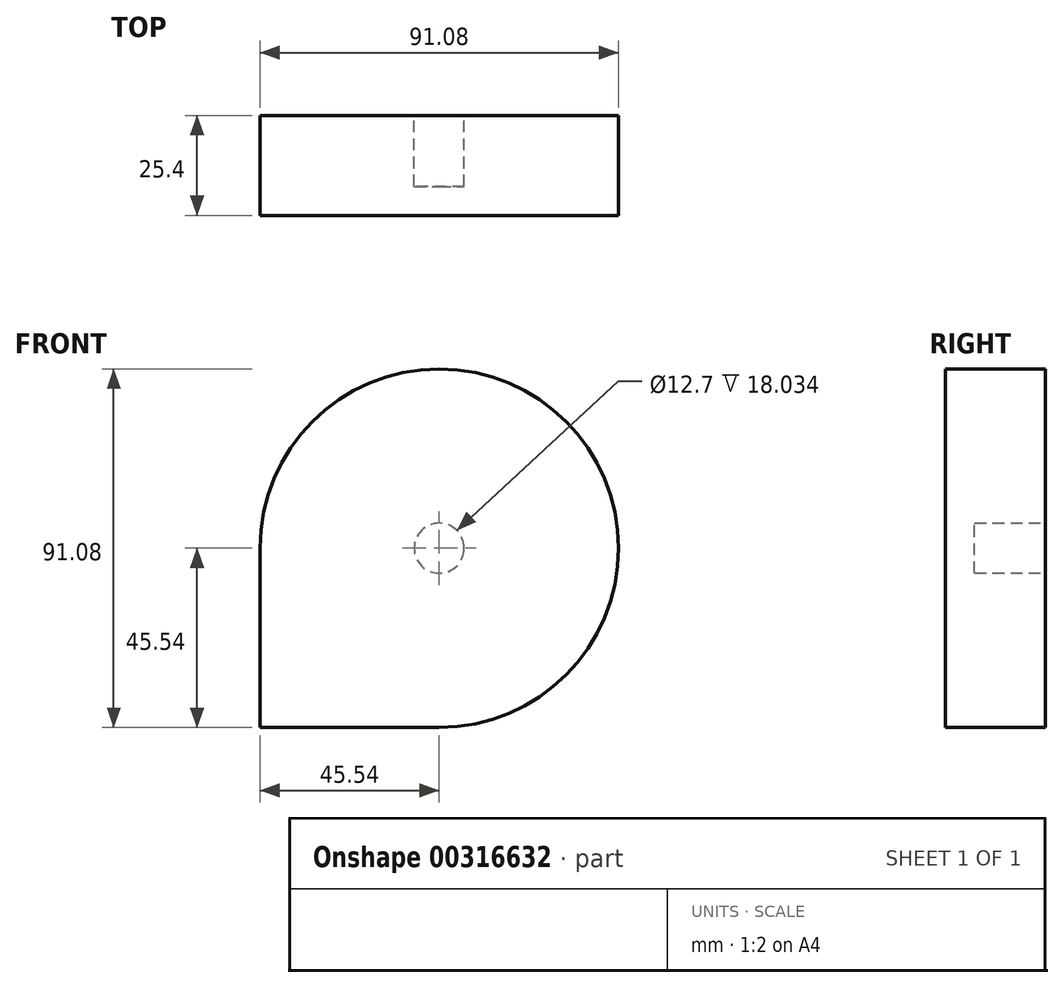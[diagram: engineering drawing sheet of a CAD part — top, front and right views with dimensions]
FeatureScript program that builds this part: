
annotation { "Feature Type Name" : "Feature", "Feature Type Description" : "" }
export const myFeature = defineFeature(function(context is Context, id is Id, definition is map)
    precondition{}
    {
        {
            var Q0;
            Q0=qCreatedBy(makeId("Front.planeOp"),FACE);
            var sketch = newSketch(context, id + "F0", { "sketchPlane" : qUnion([Q0])});
            skArc(sketch, "E0", {"start": v(0, -45.54) * mm, "mid": v(32.2, 32.2) * mm, "end": v(-45.54, 0) * mm});
            skLineSegment(sketch, "E1", {"start": v(0, -45.54) * mm, "end": v(-45.54, -45.54) * mm});
            skLineSegment(sketch, "E2", {"start": v(-45.54, -45.54) * mm, "end": v(-45.54, 0) * mm});
            skSolve(sketch);
        }
        {
            var Q0;
            Q0=makeQuery(id+"F0.imprint","IMPRINT",FACE,{"disambiguationData":[TD([[makeQuery(id+"F0.imprint","IMPRINT",EDGE,{"derivedFrom":sQuery(id+"F0.wireOp",EDGE,"E0")}),1.0]])]});
            extrude(context, id + "F1", {"entities" : qUnion([Q0]), "depth" : 25.4 * mm});
        }
        {
            var Q0;
            Q0=qCreatedBy(makeId("Front.planeOp"),FACE);
            var sketch = newSketch(context, id + "F2", { "sketchPlane" : qUnion([Q0])});
            skCircle(sketch, "E3", {"center": v(0, 0) * mm, "radius": 6.35 * mm});
            skSolve(sketch);
        }
        {
            var Q0;
            Q0 = qSketchRegion(id + "F2", true);
            extrude(context, id + "F3", {"entities" : qUnion([Q0]), "operationType" : NewBodyOperationType.REMOVE, "depth" : 18.03 * mm});
        }
    });
